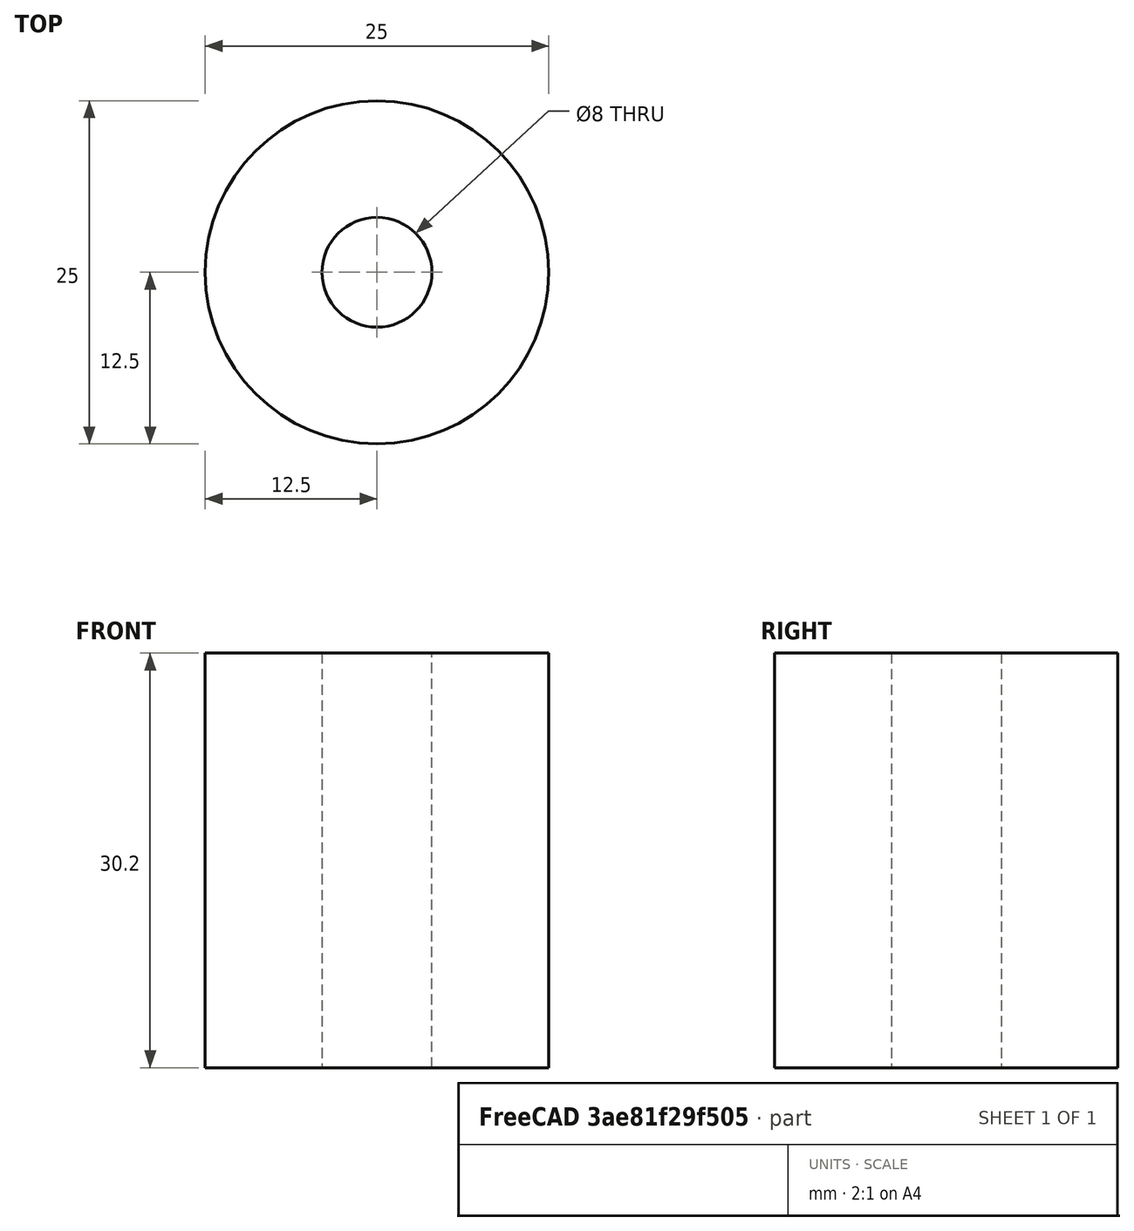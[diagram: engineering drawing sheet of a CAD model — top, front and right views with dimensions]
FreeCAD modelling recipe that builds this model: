
FCSTD DOCUMENT  (FreeCAD 1.0R39109 (Git))
Label: Тюрючек
License: All rights reserved
LicenseURL: https://en.wikipedia.org/wiki/All_rights_reserved
objects: Sketcher::SketchObject×1, PartDesign::Pad×1, PartDesign::Body×1
note: 6 computed .brp shape members not serialized (recipe doc carries the construction recipe); baked Part::Feature solids carry a one-line shape summary decoded from their .brp

FEATURE [Sketcher::SketchObject] Sketch
  ArcFitTolerance = 1e-06
  AttachmentSupport = -> [XY_Plane]
  FullyConstrained = true
  MakeInternals = false
  MapMode = 5
  sketch-geometry (2):
    g0: Circle CenterX=0 CenterY=0 CenterZ=0 NormalX=0 NormalY=0 NormalZ=1 AngleXU=0 Radius=4
    g1: Circle CenterX=0 CenterY=0 CenterZ=0 NormalX=0 NormalY=0 NormalZ=1 AngleXU=0 Radius=12.5
  constraints (4):
    c: Diameter(g0) = 8
    c: Coincident(g0,g-1)
    c: Diameter(g1) = 25
    c: Coincident(g1,g0)
FEATURE [PartDesign::Pad] Pad
  Direction = (0,0,1)
  Length = 30.2
  Length2 = 10
  Profile = -> Sketch
  ReferenceAxis = -> Sketch [N_Axis]
  Refine = true
  Suppressed = false
  Type = 0
FEATURE [PartDesign::Body] Body  label="Тело"
  AllowCompound = false
  Group = -> [Sketch,Pad]
  Origin = -> Origin
  Tip = -> Pad
